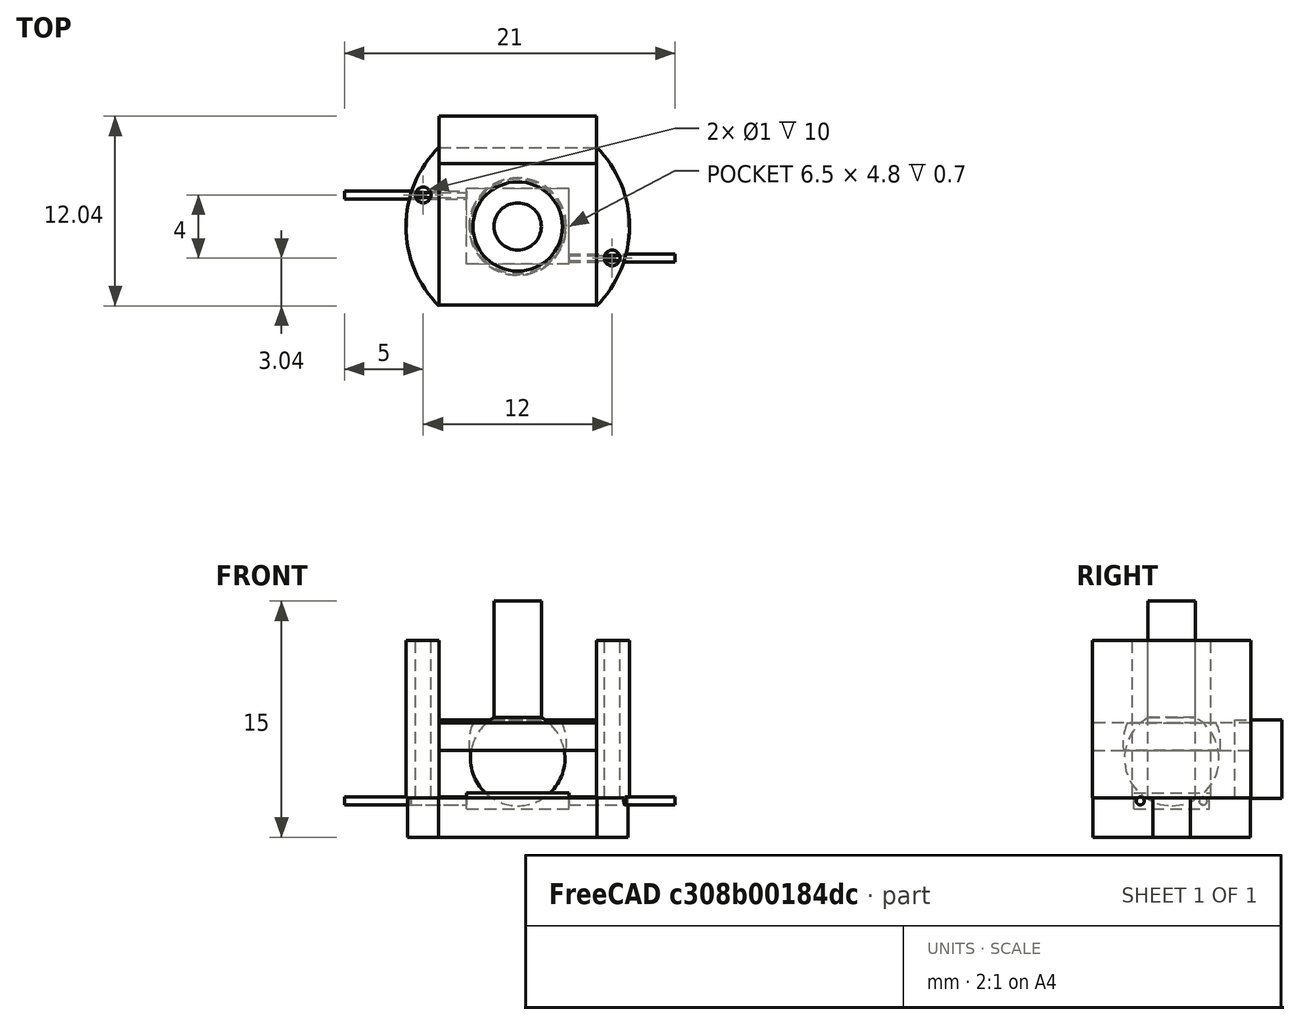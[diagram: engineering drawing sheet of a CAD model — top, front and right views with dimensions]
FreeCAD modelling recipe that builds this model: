
FCSTD DOCUMENT  (FreeCAD 0.16R6710 (Git))
Label: Feet sensors0.3
License: All rights reserved
LicenseURL: http://en.wikipedia.org/wiki/All_rights_reserved
objects: Part::Cylinder×11, Part::Box×8, Part::Cut×8, Part::Fuse×7, Part::MultiCommon×3, Part::Sphere×2
note: 39 computed .brp shape members not serialized (recipe doc carries the construction recipe); baked Part::Feature solids carry a one-line shape summary decoded from their .brp

FEATURE [Part::Sphere] Sphere
  Angle1 = -90
  Angle2 = 90
  Angle3 = 360
  Radius = 3
FEATURE [Part::Cylinder] Cylinder
  Angle = 360
  Height = 10
  Radius = 1.5
FEATURE [Part::Box] Box  label="Cube"
  Height = 1
  Length = 6.5
  Placement = pos=(-3.25,-2.4,-4.2) rot=(0,0,1;0rad)
  Width = 4.8
FEATURE [Part::Cylinder] Cylinder001
  Angle = 360
  Height = 10
  Placement = pos=(-11,2,-3.7) rot=(0,1,0;1.5708rad)
  Radius = 0.25
FEATURE [Part::Cylinder] Cylinder002
  Angle = 360
  Height = 10
  Placement = pos=(0,-2,-3.7) rot=(0,1,0;1.5708rad)
  Radius = 0.25
FEATURE [Part::Box] Box001  label="Cube001"
  Height = 7.25
  Length = 14
  Placement = pos=(-7,-5,-6) rot=(0,0,1;0rad)
  Width = 10
FEATURE [Part::Box] Box002  label="Cube002"
  Height = 1
  Length = 6.5
  Placement = pos=(-3.25,-2.4,-4.2) rot=(0,0,1;0rad)
  Width = 4.8
FEATURE [Part::Cylinder] Cylinder003
  Angle = 360
  Height = 10
  Placement = pos=(-11,2,-3.7) rot=(0,1,0;1.5708rad)
  Radius = 0.25
FEATURE [Part::Cylinder] Cylinder004
  Angle = 360
  Height = 10
  Placement = pos=(0,-2,-3.7) rot=(0,1,0;1.5708rad)
  Radius = 0.25
FEATURE [Part::Fuse] Fusion
  Base = -> Cylinder003
  Tool = -> Cylinder004
FEATURE [Part::Fuse] Fusion001
  Base = -> Box002
  Tool = -> Fusion
FEATURE [Part::Box] Box003  label="Cube003"
  Height = 3
  Length = 10
  Placement = pos=(-5,-6,-3.5) rot=(0,0,1;0rad)
  Width = 12
FEATURE [Part::Cut] Cut
  Base = -> Box001
  Tool = -> Box003
FEATURE [Part::Cut] Cut001
  Base = -> Cut
  Tool = -> Fusion001
FEATURE [Part::Fuse] Fusion002
  Base = -> Cylinder001
  Tool = -> Cylinder002
FEATURE [Part::Fuse] Fusion003  label="Switch"
  Base = -> Box
  Tool = -> Fusion002
FEATURE [Part::Box] Box004  label="Cube004"
  Height = 5
  Length = 10
  Placement = pos=(-5,4,-3.55) rot=(0,0,1;0rad)
  Width = 3
FEATURE [Part::Sphere] Sphere001
  Angle1 = -90
  Angle2 = 90
  Angle3 = 360
  Radius = 3.1
FEATURE [Part::Cylinder] Cylinder005
  Angle = 360
  Height = 10
  Placement = pos=(0,0,0.5) rot=(0,0,1;0rad)
  Radius = 2.5
FEATURE [Part::Fuse] Fusion004
  Base = -> Sphere001
  Tool = -> Cylinder005
FEATURE [Part::Cut] Cut002
  Base = -> Cut001
  Tool = -> Fusion004
FEATURE [Part::Fuse] Fusion005  label="Ball and Screw"
  Base = -> Sphere
  Placement = pos=(0,0,-1) rot=(0,0,1;0rad)
  Tool = -> Cylinder
FEATURE [Part::Cut] Cut003
  Base = -> Cut001
  Tool = -> Fusion004
FEATURE [Part::Box] Box005  label="Cube005"
  Height = 8
  Length = 21
  Placement = pos=(-9,-7,-3.5) rot=(0,0,1;0rad)
  Width = 17
FEATURE [Part::Box] Box006  label="Cube006"
  Height = 12
  Length = 21
  Placement = pos=(-9,-7,-3.5) rot=(0,0,1;0rad)
  Width = 17
FEATURE [Part::Cut] Cut004  label="Bottom Switch holder"
  Base = -> Cut003
  Tool = -> Box005
FEATURE [Part::MultiCommon] Common  label="Ball and screw holder"
  Shapes = -> [Cut002,Box006]
FEATURE [Part::Cylinder] Cylinder006
  Angle = 360
  Height = 10
  Placement = pos=(0,0,-3.5) rot=(0,0,1;0rad)
  Radius = 7.1
FEATURE [Part::Box] Box007  label="Cube007"
  Height = 10
  Length = 10
  Placement = pos=(-5,-9,-3.5) rot=(0,0,1;0rad)
  Width = 20
FEATURE [Part::Cut] Cut005
  Base = -> Cylinder006
  Tool = -> Box007
FEATURE [Part::Cylinder] Cylinder007
  Angle = 360
  Height = 10
  Placement = pos=(0,0,-3.5) rot=(0,0,1;0rad)
  Radius = 7.1
FEATURE [Part::MultiCommon] Common001
  Shapes = -> [Common,Cylinder007]
FEATURE [Part::Fuse] Fusion006
  Base = -> Cut005
  Tool = -> Common001
FEATURE [Part::Cylinder] Cylinder008
  Angle = 360
  Height = 10
  Placement = pos=(0,0,-6.5) rot=(0,0,1;0rad)
  Radius = 7.1
FEATURE [Part::MultiCommon] Common002
  Shapes = -> [Cut004,Cylinder008]
FEATURE [Part::Cylinder] Cylinder009
  Angle = 360
  Height = 13
  Placement = pos=(-6,2,-4) rot=(0,0,1;0rad)
  Radius = 0.5
FEATURE [Part::Cut] Cut006
  Base = -> Fusion006
  Tool = -> Cylinder009
FEATURE [Part::Cylinder] Cylinder010
  Angle = 360
  Height = 13
  Placement = pos=(6,-2,-4) rot=(0,0,1;0rad)
  Radius = 0.5
FEATURE [Part::Cut] Cut007
  Base = -> Cut006
  Tool = -> Cylinder010
